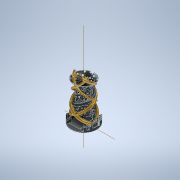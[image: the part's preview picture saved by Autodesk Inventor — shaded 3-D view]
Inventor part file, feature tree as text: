
AUTODESK INVENTOR PART (.ipt)
format: ipt  version: 2022 (Build 260153000, 153)  size: 7,433,216 bytes
history: native  units: mm
features: sketch x27, extrude x26, helix x5, plane x4, fillet x3, revolve x2, pattern_circular x2, chamfer x2
ambient origin geometry x8: Origin, YZ Plane, XZ Plane, XY Plane, X Axis, Y Axis, Z Axis, Center Point
bodies: Solid1 (feature_tree)
feature tree (71):
  revolve  "Revolution1"  [1 undecoded]
  plane  "Work Plane1"
  extrude  "Extrusion4"  Depth=20.0mm
  extrude  "Extrusion2"  Depth=19.0mm
  pattern_circular  "Circular Pattern2"  Count=9  [1 undecoded]
  plane  "Work Plane3"
  extrude  "Extrusion3"  Depth=10.0mm
  pattern_circular  "Circular Pattern3"  Count=7  [1 undecoded]
  helix  "Coil1"  [1 undecoded]
  helix  "Coil2"  [1 undecoded]
  helix  "Coil3"  [1 undecoded]
  helix  "Coil4"  [1 undecoded]
  helix  "Coil5"  [1 undecoded]
  extrude  "Extrusion5"  Depth=20.0mm
  revolve  "Revolution2"  [1 undecoded]
  extrude  "Extrusion6"  Depth=30.0mm
  extrude  "Extrusion15"  Depth=15.0mm
  extrude  "Extrusion16"  Depth=30.0mm
  extrude  "Extrusion17"  Depth=45.0mm
  extrude  "Extrusion18"  Depth=13.0mm
  extrude  "Extrusion19"  Depth=39.0mm
  extrude  "Extrusion20"  Depth=11.0mm
  extrude  "Extrusion21"  Depth=10.0mm
  extrude  "Extrusion22"  Depth=11.0mm
  extrude  "Extrusion23"  Depth=9.0mm
  extrude  "Extrusion25"  Depth=3.0mm TaperAngle=0.0deg
  extrude  "Extrusion26"  Depth=54.0mm TaperAngle=0.0deg
  extrude  "Extrusion27"  Depth=35.0mm
  extrude  "Extrusion28"  Depth=30.0mm
  extrude  "Extrusion29"  Depth=30.0mm
  extrude  "Extrusion30"  Depth=35.0mm
  extrude  "Extrusion31"  Depth=35.0mm
  plane  "Work Plane4"
  extrude  "Extrusion32"  Depth=5.0mm
  extrude  "Extrusion33"  Depth=10.0mm TaperAngle=0.0deg
  chamfer  "Chamfer2"  Distance=5.0mm
  chamfer  "Chamfer3"  Distance=10.0mm
  fillet  "Fillet5"  Radius=15.0mm
  fillet  "Fillet6"  Radius=0.2mm
  extrude  "Extrusion34"  Depth=5.0mm TaperAngle=0.0deg
  fillet  "Fillet16"  Radius=10.0mm
  extrude  "Extrusion35"  Depth=15.0mm TaperAngle=0.0deg
  extrude  "Extrusion36"  Depth=3.0mm TaperAngle=0.0deg
  sketch  "Sketch1"  dims[d11=50.0mm d12=40.0mm]
  sketch  "Sketch3"  dims[d13=20.0mm d14=20.0mm]
  plane  "Work Plane2"
  sketch  "Sketch4"  dims[d15=23.0mm d16=19.0mm d17=90.0mm]
  sketch  "Sketch5"  dims[d18=32.0mm d19=10.0mm]
  sketch  "Sketch7"  dims[d20=151.0mm]
  sketch  "Sketch8"  dims[d26=2.0mm]
  sketch  "Sketch9"  dims[d27=2.0mm]
  sketch  "Sketch10"  dims[d28=2.0mm]
  sketch  "Sketch11"  dims[d29=2.0mm]
  sketch  "Sketch13"  dims[d30=2.0mm]
  sketch  "Sketch16"  dims[d31=90.0deg d32=70.0mm d38=77.75mm d39=0.0mm d40=40.0mm d41=360.0deg d43=70.0mm d44=77.75mm d45=0.0mm d46=40.0mm d47=360.0deg]
  sketch  "Sketch17"  dims[d49=20.0mm d50=20.0mm]
  sketch  "Sketch20"  dims[d51=20.0mm d52=20.0mm]
  sketch  "Sketch21"  dims[d53=40.0mm d54=30.0mm]
  sketch  "Sketch22"  dims[d55=30.0mm d56=15.0mm]
  sketch  "Sketch26"  dims[d57=15.0mm d58=30.0mm]
  sketch  "Sketch27"  dims[d59=77.75mm d60=0.0mm d61=45.0mm]
  sketch  "Sketch28"  dims[d62=35.0mm]
  sketch  "Sketch30"  dims[d63=70.0mm d64=100.0mm d65=10.0mm d66=-0.567232mm d67=90.0deg d68=90.0deg d69=90.0deg d70=90.0deg d71=13.0mm]
  sketch  "Sketch31"  dims[d72=10.0mm d73=39.0mm]
  sketch  "Sketch33"  dims[d74=140.0mm d75=160.0mm d76=10.0mm d77=-0.645772mm d78=90.0deg d79=90.0deg d80=90.0deg d81=90.0deg d82=11.0mm]
  sketch  "Sketch35"  dims[d83=39.0mm d84=10.0mm]
  sketch  "Sketch37"  dims[d85=135.0mm d86=160.0mm d87=10.0mm d88=-0.645772mm d89=90.0deg d90=90.0deg d91=90.0deg d92=90.0deg d93=11.0mm]
  sketch  "Sketch41"  dims[d94=170.0mm d95=160.0mm d96=10.0mm d97=-0.645772mm d98=90.0deg d99=90.0deg d100=90.0deg d101=90.0deg d102=9.0mm]
  sketch  "Sketch43"  dims[d103=170.0mm d104=160.0mm d105=10.0mm d106=-0.645772mm d107=90.0deg d108=90.0deg d109=90.0deg d110=90.0deg d125=3.0mm d126=0.0mm]
  sketch  "Sketch44"  dims[d130=270.0deg d133=54.0mm d134=0.0mm]
  sketch  "Sketch45"  dims[d141=35.0mm d165=35.0mm d166=30.0mm d167=30.0mm d168=30.0mm d169=30.0mm d170=35.0mm d172=35.0mm d186=5.0mm d187=10.0mm d188=0.0mm d190=5.0mm d191=0.0mm d192=10.0mm d193=0.0mm d194=15.0mm d195=0.0mm d196=0.2mm d197=0.0mm d198=5.0mm d199=0.0mm d200=10.0mm d201=0.0mm d202=15.0mm d203=0.0mm d204=3.0mm d205=0.0mm d210=1.0mm d211=0.0mm d213=10.0mm d214=0.0mm d218=30.0mm d219=23.5mm d220=5.75mm d221=5.75mm d222=5.75mm d223=14.0mm d224=0.0mm d225=22.5mm d226=6.25mm d227=6.25mm d228=6.25mm d229=14.0mm d230=0.0mm d235=14.0mm d236=0.0mm d241=10.0mm d242=0.0mm d245=17.5mm d251=10.0mm d252=0.0mm d254=21.0mm d258=24.0mm d259=0.0mm d263=25.0mm d266=5.0mm d267=5.0mm d268=12.0mm d269=0.0mm d270=11.0mm d271=2.0mm d272=45.0deg d273=12.0mm d274=2.0mm d275=45.0deg d276=35.0mm d278=5.0mm d279=5.0mm d280=5.0mm d282=2.0mm d283=1.0mm d292=20.0mm d293=0.0mm d295=2.0mm d299=25.0mm d300=52.0mm d301=54.0mm d302=0.0mm d303=25.0mm d304=5.0mm d305=5.0mm d306=5.0mm d307=5.0mm d308=26.0mm d309=3.0mm d310=2.0mm d311=2.484774mm d312=17.5mm d313=21.0mm d314=0.0mm d315=60.0mm d316=200.0mm d317=0.0mm d132=0.0mm d135=0.0mm]
note: 9 required parameter values undecoded (feature->parameter linkage not recoverable at this tier; creation-order binding heuristic only, values carry confidence <= 0.55)